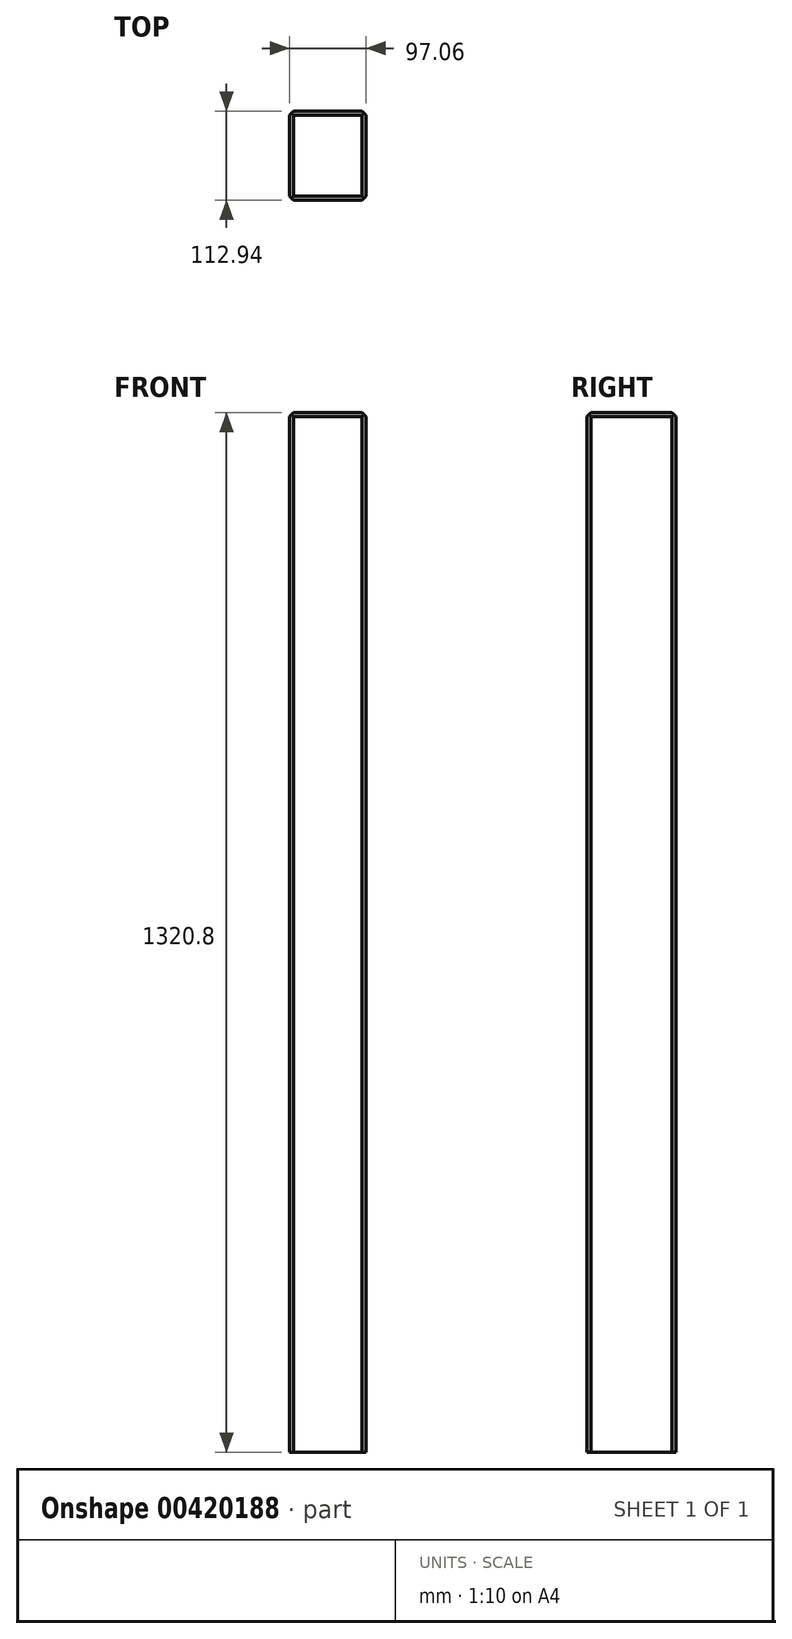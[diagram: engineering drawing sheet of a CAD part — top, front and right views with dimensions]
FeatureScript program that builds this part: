
annotation { "Feature Type Name" : "Feature", "Feature Type Description" : "" }
export const myFeature = defineFeature(function(context is Context, id is Id, definition is map)
    precondition{}
    {
        {
            var Q0;
            Q0=qCreatedBy(makeId("Top.planeOp"),FACE);
            var sketch = newSketch(context, id + "F0", { "sketchPlane" : qUnion([Q0])});
            skLineSegment(sketch, "E0.bottom", {"start": v(48.53, 56.47) * mm, "end": v(-48.53, 56.47) * mm});
            skLineSegment(sketch, "E0.top", {"start": v(48.53, -56.47) * mm, "end": v(-48.53, -56.47) * mm});
            skLineSegment(sketch, "E0.left", {"start": v(48.53, 56.47) * mm, "end": v(48.53, -56.47) * mm});
            skLineSegment(sketch, "E0.right", {"start": v(-48.53, 56.47) * mm, "end": v(-48.53, -56.47) * mm});
            skPoint(sketch, "E0.middle", {"position": v(0, 0) * mm});
            skSolve(sketch);
        }
        {
            var Q0;
            Q0 = qSketchRegion(id + "F0", true);
            extrude(context, id + "F1", {"entities" : qUnion([Q0]), "depth" : 88.9 * mm, "hasSecondDirection" : true, "secondDirectionOppositeDirection" : true, "secondDirectionDepth" : 1231.9 * mm});
        }
        {
            var Q0;
            Q0=makeQuery(id+"F1.opExtrude","SWEPT_EDGE",EDGE,{"disambiguationData":[OSD([sQuery(id+"F0.wireOp",EDGE,"E0.top"),sQuery(id+"F0.wireOp",EDGE,"E0.left")])]});
            chamfer(context, id + "F2", {"entities" : qUnion([Q0]), "width" : 5.08 * mm, "tangentPropagation" : true});
        }
        {
            var Q0;
            Q0=makeQuery(id+"F1.opExtrude","SWEPT_EDGE",EDGE,{"disambiguationData":[OSD([sQuery(id+"F0.wireOp",EDGE,"E0.top"),sQuery(id+"F0.wireOp",EDGE,"E0.right")])]});
            chamfer(context, id + "F3", {"entities" : qUnion([Q0]), "width" : 5.08 * mm, "tangentPropagation" : true});
        }
        {
            var Q0;
            Q0=makeQuery(id+"F1.opExtrude","SWEPT_EDGE",EDGE,{"disambiguationData":[OSD([sQuery(id+"F0.wireOp",EDGE,"E0.bottom"),sQuery(id+"F0.wireOp",EDGE,"E0.right")])]});
            chamfer(context, id + "F4", {"entities" : qUnion([Q0]), "width" : 5.08 * mm, "tangentPropagation" : true});
        }
        {
            var Q0;
            Q0=makeQuery(id+"F1.opExtrude","SWEPT_EDGE",EDGE,{"disambiguationData":[OSD([sQuery(id+"F0.wireOp",EDGE,"E0.bottom"),sQuery(id+"F0.wireOp",EDGE,"E0.left")])]});
            chamfer(context, id + "F5", {"entities" : qUnion([Q0]), "width" : 5.08 * mm, "tangentPropagation" : true});
        }
        {
            var Q0;
            Q0=makeQuery(id+"F1.opExtrude","CAP_EDGE",EDGE,{"disambiguationData":[OSD([sQuery(id+"F0.wireOp",EDGE,"E0.bottom")])],"isStart":false});
            chamfer(context, id + "F6", {"entities" : qUnion([Q0]), "width" : 5.08 * mm, "tangentPropagation" : true});
        }
        {
            var Q0;
            Q0=makeQuery(id+"F1.opExtrude","CAP_EDGE",EDGE,{"disambiguationData":[OSD([sQuery(id+"F0.wireOp",EDGE,"E0.left")])],"isStart":false});
            chamfer(context, id + "F7", {"entities" : qUnion([Q0]), "width" : 5.08 * mm, "tangentPropagation" : true});
        }
        {
            var Q0;
            Q0=makeQuery(id+"F1.opExtrude","CAP_EDGE",EDGE,{"disambiguationData":[OSD([sQuery(id+"F0.wireOp",EDGE,"E0.top")])],"isStart":false});
            chamfer(context, id + "F8", {"entities" : qUnion([Q0]), "width" : 5.08 * mm, "tangentPropagation" : true});
        }
        {
            var Q0;
            Q0=makeQuery(id+"F1.opExtrude","CAP_EDGE",EDGE,{"disambiguationData":[OSD([sQuery(id+"F0.wireOp",EDGE,"E0.right")])],"isStart":false});
            chamfer(context, id + "F9", {"entities" : qUnion([Q0]), "width" : 5.08 * mm, "tangentPropagation" : true});
        }
    });
